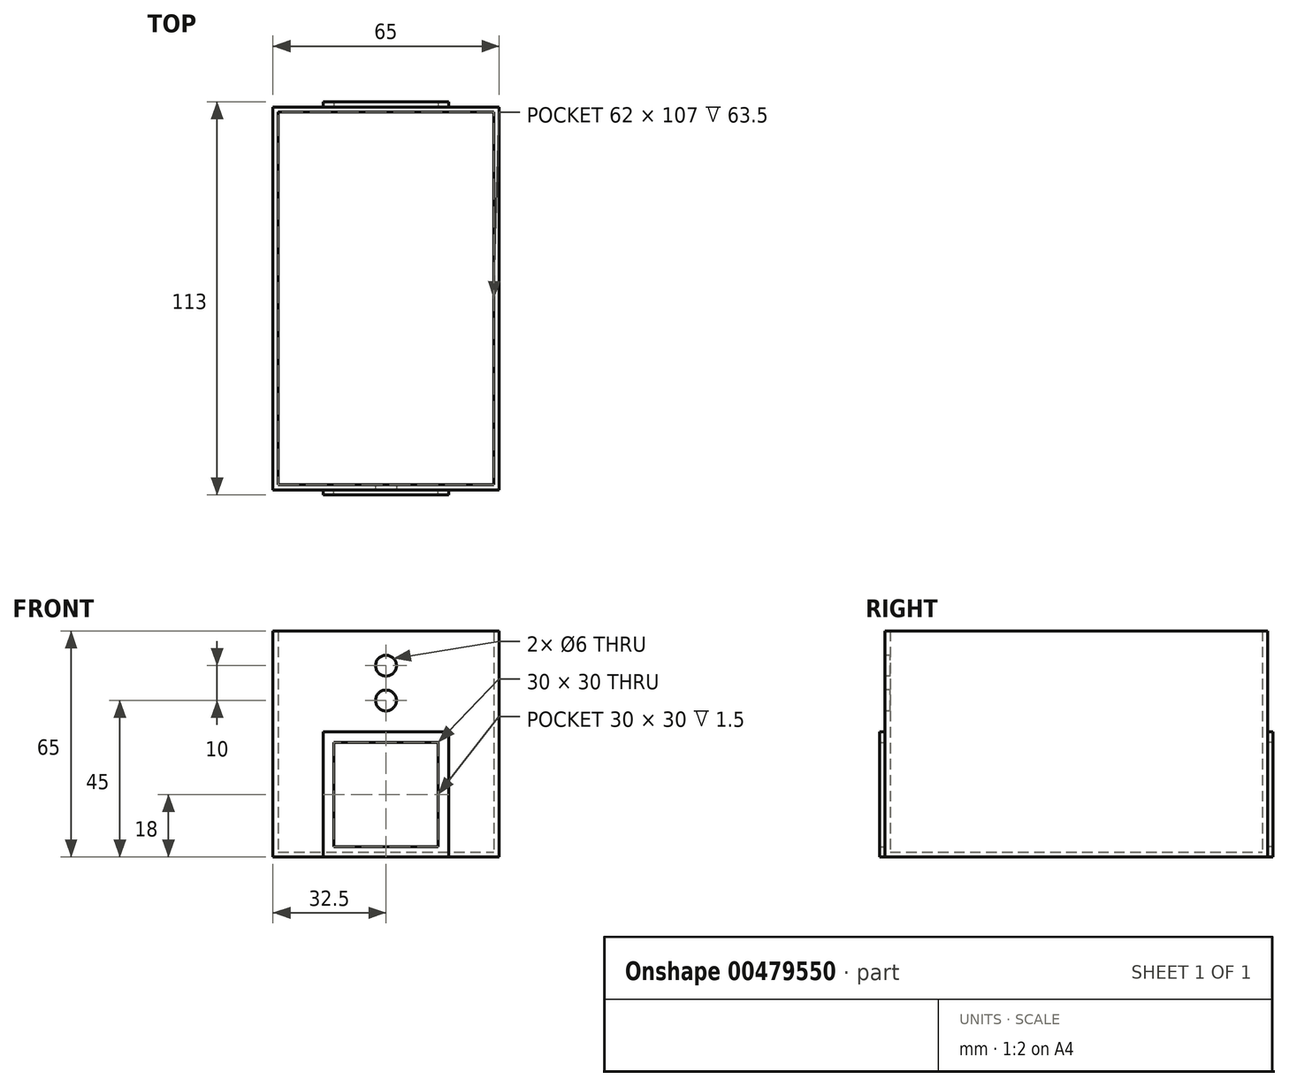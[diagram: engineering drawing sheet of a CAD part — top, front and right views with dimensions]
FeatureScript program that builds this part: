
annotation { "Feature Type Name" : "Feature", "Feature Type Description" : "" }
export const myFeature = defineFeature(function(context is Context, id is Id, definition is map)
    precondition{}
    {
        {
            var Q0;
            Q0=qCreatedBy(makeId("Front.planeOp"),FACE);
            var sketch = newSketch(context, id + "F0", { "sketchPlane" : qUnion([Q0])});
            skLineSegment(sketch, "E0.bottom", {"start": v(-32.5, 65) * mm, "end": v(32.5, 65) * mm});
            skLineSegment(sketch, "E0.top", {"start": v(-32.5, 0) * mm, "end": v(32.5, 0) * mm});
            skLineSegment(sketch, "E0.left", {"start": v(-32.5, 65) * mm, "end": v(-32.5, 0) * mm});
            skLineSegment(sketch, "E0.right", {"start": v(32.5, 65) * mm, "end": v(32.5, 0) * mm});
            skSolve(sketch);
        }
        {
            var Q0;
            Q0=makeQuery(id+"F0.imprint","IMPRINT",FACE,{"disambiguationData":[TD([[makeQuery(id+"F0.imprint","IMPRINT",EDGE,{"derivedFrom":sQuery(id+"F0.wireOp",EDGE,"E0.bottom")}),-1.0]])]});
            extrude(context, id + "F1", {"entities" : qUnion([Q0]), "depth" : 55 * mm});
        }
        {
            var Q0;
            Q0=makeQuery(id+"F1.opExtrude","CAP_FACE",FACE,{"disambiguationData":[OSD([sQuery(id+"F0.wireOp",EDGE,"E0.bottom"),sQuery(id+"F0.wireOp",EDGE,"E0.top"),sQuery(id+"F0.wireOp",EDGE,"E0.left"),sQuery(id+"F0.wireOp",EDGE,"E0.right")])],"isStart":false});
            var sketch = newSketch(context, id + "F2", { "sketchPlane" : qUnion([Q0])});
            skLineSegment(sketch, "E1.bottom", {"start": v(-18, 36) * mm, "end": v(18, 36) * mm});
            skLineSegment(sketch, "E1.top", {"start": v(-18, 0) * mm, "end": v(18, 0) * mm});
            skLineSegment(sketch, "E1.left", {"start": v(-18, 36) * mm, "end": v(-18, 0) * mm});
            skLineSegment(sketch, "E1.right", {"start": v(18, 36) * mm, "end": v(18, 0) * mm});
            skLineSegment(sketch, "E2.bottom", {"start": v(-15, 33) * mm, "end": v(15, 33) * mm});
            skLineSegment(sketch, "E2.top", {"start": v(-15, 3) * mm, "end": v(15, 3) * mm});
            skLineSegment(sketch, "E2.left", {"start": v(-15, 33) * mm, "end": v(-15, 3) * mm});
            skLineSegment(sketch, "E2.right", {"start": v(15, 33) * mm, "end": v(15, 3) * mm});
            skSolve(sketch);
        }
        {
            var Q0;
            Q0 = qSketchRegion(id + "F2", true);
            extrude(context, id + "F3", {"entities" : qUnion([Q0]), "operationType" : NewBodyOperationType.ADD, "depth" : 1.5 * mm});
        }
        {
            var Q0;
            Q0=makeQuery(id+"F1.opExtrude","SWEPT_BODY",BODY,{"disambiguationData":[OSD([sQuery(id+"F0.wireOp",EDGE,"E0.bottom"),sQuery(id+"F0.wireOp",EDGE,"E0.top"),sQuery(id+"F0.wireOp",EDGE,"E0.left"),sQuery(id+"F0.wireOp",EDGE,"E0.right")])]});
            var Q1;
            Q1=qCreatedBy(makeId("Front.planeOp"),FACE);
            mirror(context, id + "F4", {"operationType" : NewBodyOperationType.ADD, "entities" : qUnion([Q0]), "mirrorPlane" : qUnion([Q1])});
        }
        {
            var Q0;
            {var subQ0=makeQuery(id+"F1.opExtrude","SWEPT_FACE",FACE,{"disambiguationData":[OSD([sQuery(id+"F0.wireOp",EDGE,"E0.bottom")])]});Q0=makeQuery(id+"F4.boolean.opBoolean","MERGE",FACE,{"derivedFrom":[subQ0,makeQuery(id+"F4.opPattern","COPY",FACE,{"derivedFrom":subQ0,"instanceName":"1"})]});}
            shell(context, id + "F5", {"entities" : qUnion([Q0]), "thickness" : 1.5 * mm});
        }
        {
            var Q0;
            {var subQ0=sQuery(id+"F0.wireOp",EDGE,"E0.left");var subQ1=sQuery(id+"F0.wireOp",EDGE,"E0.top");var subQ2=sQuery(id+"F0.wireOp",EDGE,"E0.right");var subQ3=sQuery(id+"F0.wireOp",EDGE,"E0.bottom");Q0=makeQuery(id+"F3.boolean.opBoolean","SPLIT",FACE,{"disambiguationData":[TD([makeQuery(id+"F1.opExtrude","SWEPT_FACE",FACE,{"disambiguationData":[OSD([subQ3])]})])],"derivedFrom":makeQuery(id+"F1.opExtrude","CAP_FACE",FACE,{"disambiguationData":[OSD([subQ3,subQ1,subQ0,subQ2])],"isStart":false})});}
            var sketch = newSketch(context, id + "F6", { "sketchPlane" : qUnion([Q0])});
            skCircle(sketch, "E3", {"center": v(0, 55) * mm, "radius": 3 * mm});
            skCircle(sketch, "E4", {"center": v(0, 45) * mm, "radius": 3 * mm});
            skSolve(sketch);
        }
        {
            var Q0;
            Q0 = qSketchRegion(id + "F6", true);
            extrude(context, id + "F7", {"entities" : qUnion([Q0]), "operationType" : NewBodyOperationType.REMOVE, "endBound" : BoundingType.UP_TO_NEXT, "oppositeDirection" : true, "depth" : 25 * mm});
        }
    });
